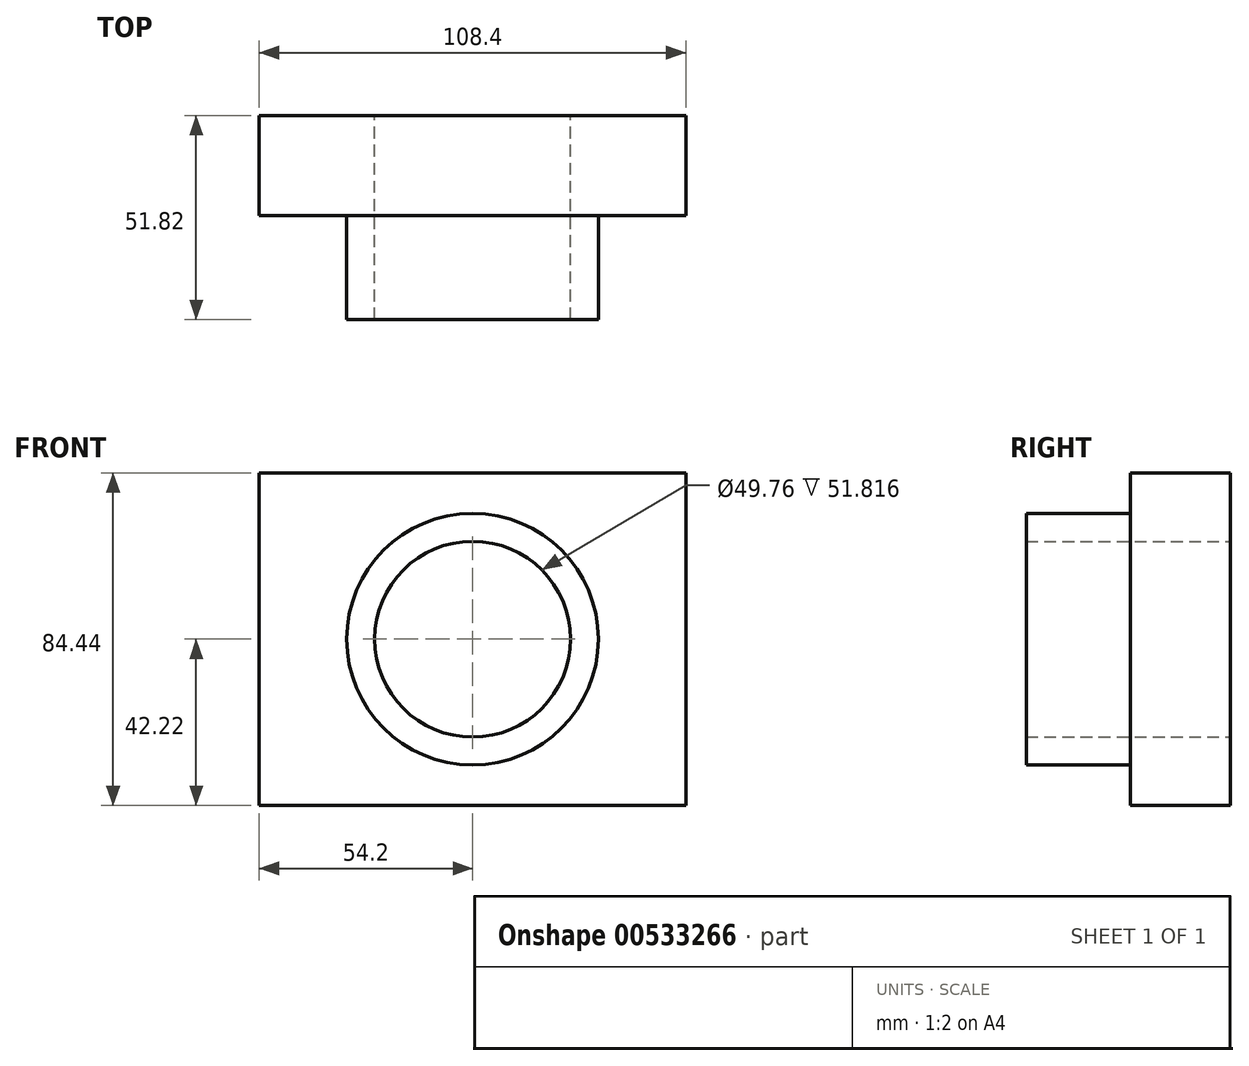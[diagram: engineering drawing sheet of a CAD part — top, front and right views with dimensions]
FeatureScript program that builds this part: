
annotation { "Feature Type Name" : "Feature", "Feature Type Description" : "" }
export const myFeature = defineFeature(function(context is Context, id is Id, definition is map)
    precondition{}
    {
        {
            var Q0;
            Q0=qCreatedBy(makeId("Front.planeOp"),FACE);
            var sketch = newSketch(context, id + "F0", { "sketchPlane" : qUnion([Q0])});
            skLineSegment(sketch, "E0.bottom", {"start": v(54.2, -42.22) * mm, "end": v(-54.2, -42.22) * mm});
            skLineSegment(sketch, "E0.top", {"start": v(54.2, 42.22) * mm, "end": v(-54.2, 42.22) * mm});
            skLineSegment(sketch, "E0.left", {"start": v(54.2, -42.22) * mm, "end": v(54.2, 42.22) * mm});
            skLineSegment(sketch, "E0.right", {"start": v(-54.2, -42.22) * mm, "end": v(-54.2, 42.22) * mm});
            skPoint(sketch, "E0.middle", {"position": v(0, 0) * mm});
            skCircle(sketch, "E1", {"center": v(0, 0) * mm, "radius": 24.88 * mm});
            skCircle(sketch, "E2", {"center": v(0, 0) * mm, "radius": 31.97 * mm});
            skSolve(sketch);
        }
        {
            var Q0;
            Q0=makeQuery(id+"F0.imprint","IMPRINT",FACE,{"disambiguationData":[TD([[makeQuery(id+"F0.imprint","IMPRINT",EDGE,{"derivedFrom":sQuery(id+"F0.wireOp",EDGE,"E1")}),-1.0]])]});
            extrude(context, id + "F1", {"entities" : qUnion([Q0]), "depth" : 51.82 * mm, "offsetDistance" : 25.4 * mm});
        }
        {
            var Q0;
            Q0 = qSketchRegion(id + "F0", true);
            extrude(context, id + "F2", {"entities" : qUnion([Q0]), "operationType" : NewBodyOperationType.ADD, "depth" : 25.4 * mm, "offsetDistance" : 25.4 * mm});
        }
    });
